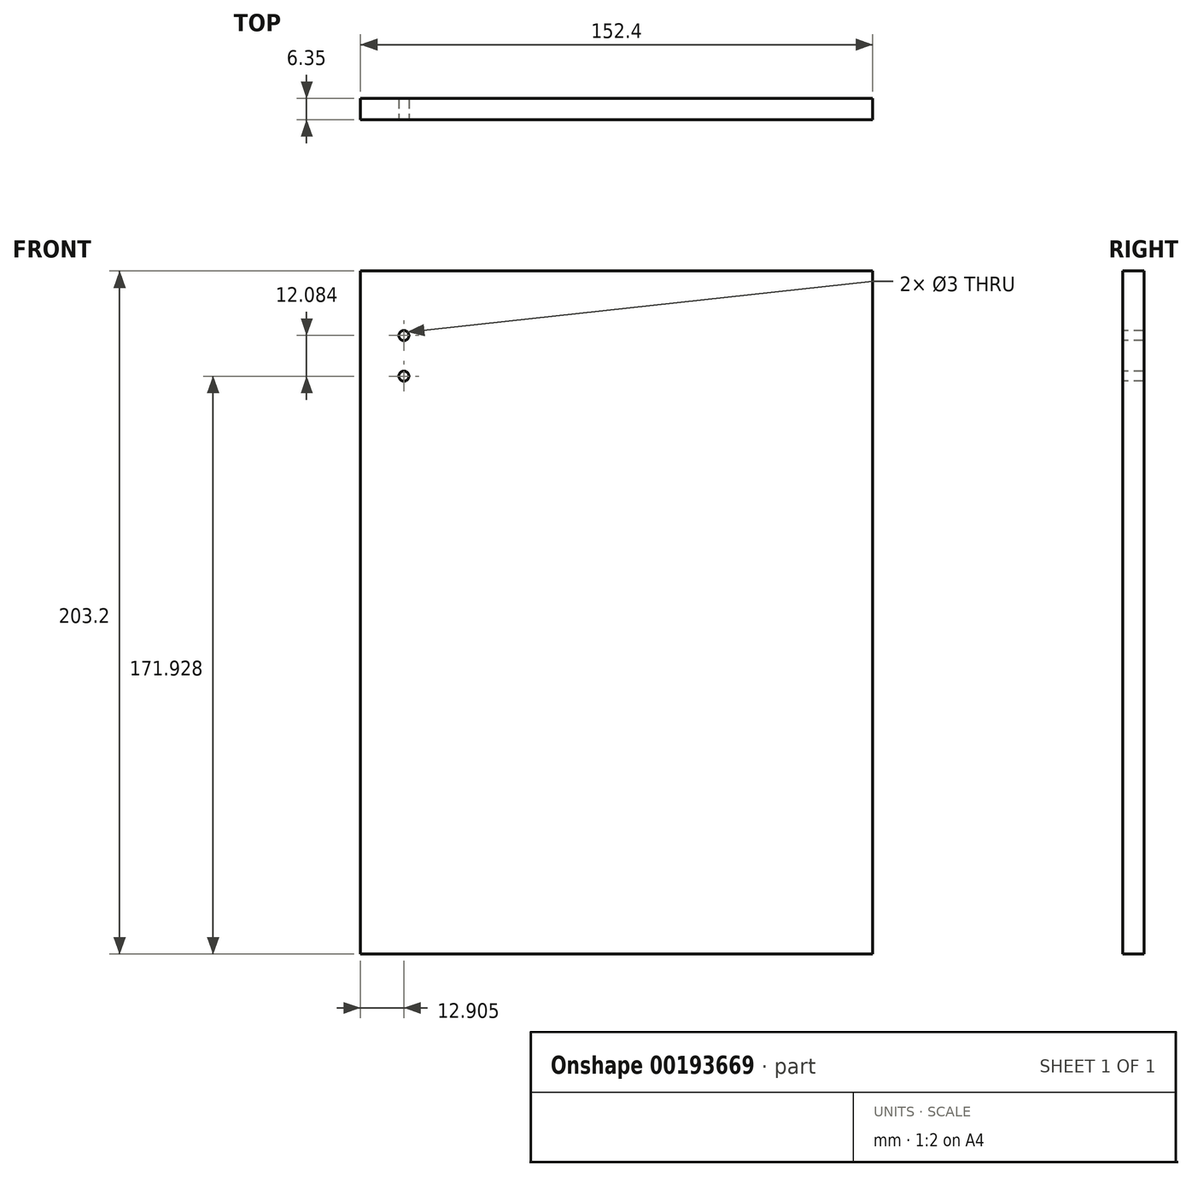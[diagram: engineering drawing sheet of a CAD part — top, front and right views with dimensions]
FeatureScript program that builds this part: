
annotation { "Feature Type Name" : "Feature", "Feature Type Description" : "" }
export const myFeature = defineFeature(function(context is Context, id is Id, definition is map)
    precondition{}
    {
        {
            var Q0;
            Q0=qCreatedBy(makeId("Front.planeOp"),FACE);
            var sketch = newSketch(context, id + "F0", { "sketchPlane" : qUnion([Q0])});
            skLineSegment(sketch, "E0.bottom", {"start": v(76.2, 101.6) * mm, "end": v(-76.2, 101.6) * mm});
            skLineSegment(sketch, "E0.top", {"start": v(76.2, -101.6) * mm, "end": v(-76.2, -101.6) * mm});
            skLineSegment(sketch, "E0.left", {"start": v(76.2, 101.6) * mm, "end": v(76.2, -101.6) * mm});
            skLineSegment(sketch, "E0.right", {"start": v(-76.2, 101.6) * mm, "end": v(-76.2, -101.6) * mm});
            skPoint(sketch, "E0.middle", {"position": v(0, 0) * mm});
            skSolve(sketch);
        }
        {
            var Q0;
            Q0=makeQuery(id+"F0.imprint","IMPRINT",FACE,{"disambiguationData":[TD([[makeQuery(id+"F0.imprint","IMPRINT",EDGE,{"derivedFrom":sQuery(id+"F0.wireOp",EDGE,"E0.bottom")}),1.0]])]});
            extrude(context, id + "F1", {"entities" : qUnion([Q0]), "depth" : 6.35 * mm});
        }
        {
            var Q0;
            Q0=makeQuery(id+"F1.opExtrude","CAP_FACE",FACE,{"disambiguationData":[OSD([sQuery(id+"F0.wireOp",EDGE,"E0.bottom"),sQuery(id+"F0.wireOp",EDGE,"E0.top"),sQuery(id+"F0.wireOp",EDGE,"E0.left"),sQuery(id+"F0.wireOp",EDGE,"E0.right")])],"isStart":false});
            var sketch = newSketch(context, id + "F2", { "sketchPlane" : qUnion([Q0])});
            skLineSegment(sketch, "E1", {"start": v(-63.5, 101.6) * mm, "end": v(-63.5, 82.55) * mm});
            skLineSegment(sketch, "E2", {"start": v(-63.5, 82.55) * mm, "end": v(-63.5, 69.85) * mm});
            skSolve(sketch);
        }
        {
            var Q0;
            Q0=makeQuery(id+"F2.imprint","IMPRINT",FACE,{"disambiguationData":[TD([[makeQuery(id+"F2.imprint","IMPRINT",EDGE,{"derivedFrom":makeQuery(id+"F1.opExtrude","CAP_EDGE",EDGE,{"disambiguationData":[OSD([sQuery(id+"F0.wireOp",EDGE,"E0.top")])],"isStart":false})}),-1.0]])]});
            var sketch = newSketch(context, id + "F3", { "sketchPlane" : qUnion([Q0])});
            skCircle(sketch, "E3", {"center": v(-63.3, 82.41) * mm, "radius": 1.5 * mm});
            skCircle(sketch, "E4", {"center": v(-63.3, 70.33) * mm, "radius": 1.5 * mm});
            skSolve(sketch);
        }
        {
            var Q0;
            Q0 = qSketchRegion(id + "F3", true);
            extrude(context, id + "F4", {"entities" : qUnion([Q0]), "operationType" : NewBodyOperationType.REMOVE, "oppositeDirection" : true, "depth" : 25 * mm});
        }
    });
